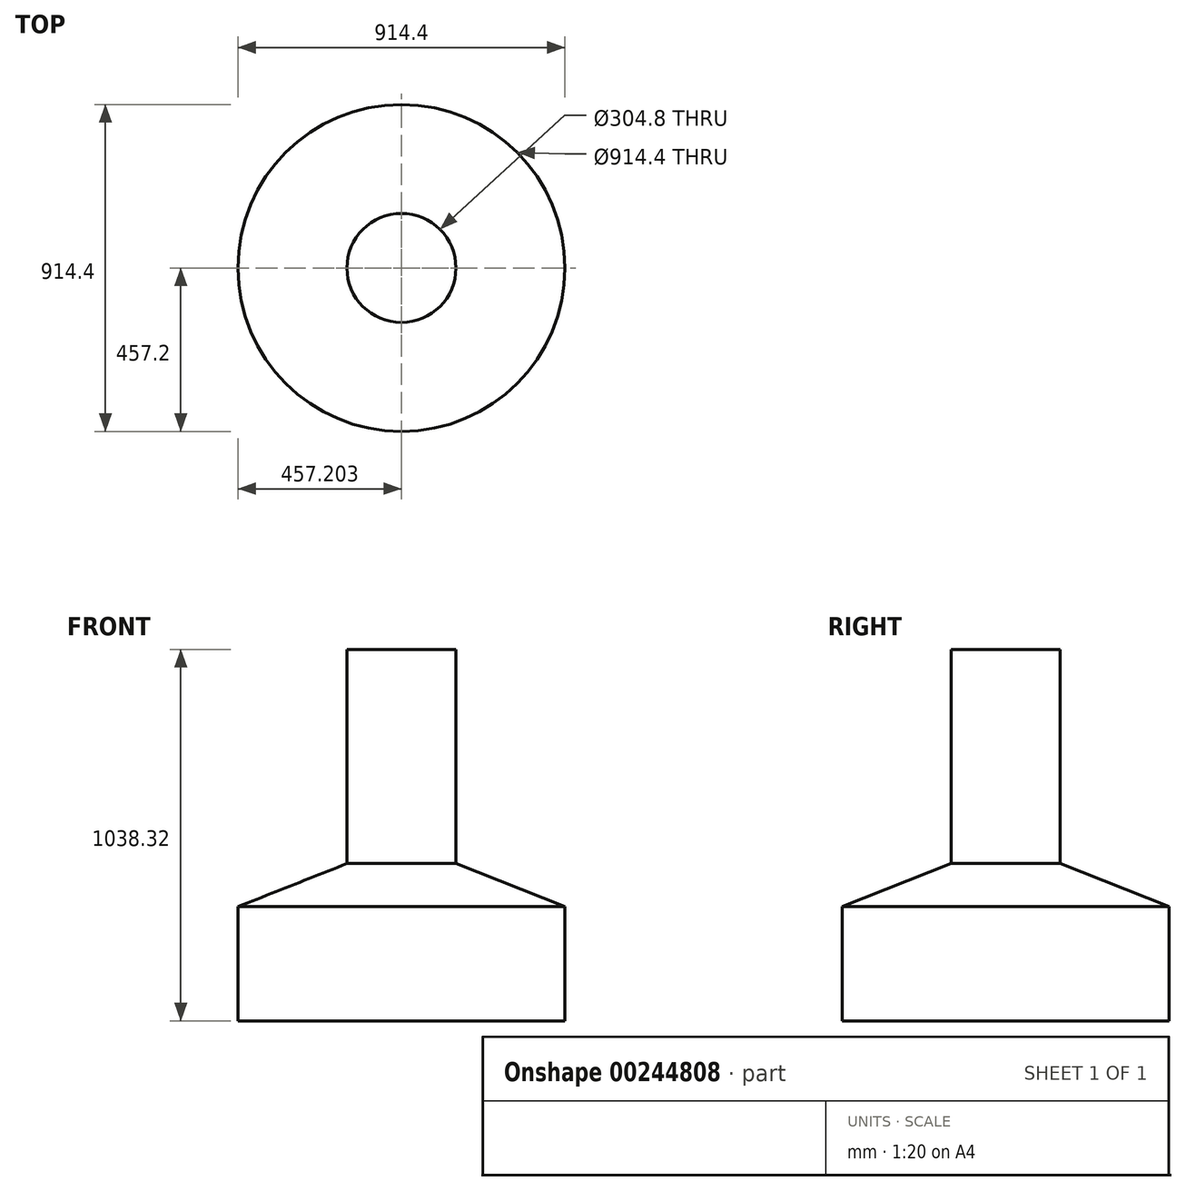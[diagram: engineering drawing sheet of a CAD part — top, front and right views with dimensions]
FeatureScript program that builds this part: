
annotation { "Feature Type Name" : "Feature", "Feature Type Description" : "" }
export const myFeature = defineFeature(function(context is Context, id is Id, definition is map)
    precondition{}
    {
        {
            var Q0;
            Q0=qCreatedBy(makeId("Front.planeOp"),FACE);
            var sketch = newSketch(context, id + "F0", { "sketchPlane" : qUnion([Q0])});
            skLineSegment(sketch, "E0", {"start": v(1424.14, 1865.35) * mm, "end": v(1424.14, 1266.84) * mm});
            skLineSegment(sketch, "E1", {"start": v(1119.34, 1146.38) * mm, "end": v(1119.34, 827.03) * mm});
            skLineSegment(sketch, "E2", {"start": v(1119.34, 1146.38) * mm, "end": v(1424.14, 1266.84) * mm});
            skLineSegment(sketch, "E3", {"start": v(1424.14, 1266.84) * mm, "end": v(1424.14, 691.05) * mm, "construction": true});
            skLineSegment(sketch, "E4", {"start": v(1119.34, 827.03) * mm, "end": v(1424.14, 827.03) * mm, "construction": true});
            skLineSegment(sketch, "E5", {"start": v(1576.54, 2110.2) * mm, "end": v(1576.54, 270) * mm, "construction": true});
            skLineSegment(sketch, "E6", {"start": v(1424.14, 1736.48) * mm, "end": v(1576.54, 1736.48) * mm, "construction": true});
            skSolve(sketch);
        }
        {
            var Q0;
            Q0 = qSketchRegion(id + "F0", true);
            var Q1;
            Q1=sQuery(id+"F0.wireOp",EDGE,"E0");
            var Q2;
            Q2=sQuery(id+"F0.wireOp",EDGE,"E2");
            var Q3;
            Q3=sQuery(id+"F0.wireOp",EDGE,"E1");
            var Q4;
            Q4=sQuery(id+"F0.wireOp",EDGE,"E5");
            revolve(context, id + "F1", {"bodyType" : ToolBodyType.SURFACE, "entities" : qUnion([Q0]), "surfaceEntities" : qUnion([Q1, Q2, Q3]), "axis" : qUnion([Q4]), "revolveType" : RevolveType.FULL});
        }
    });
